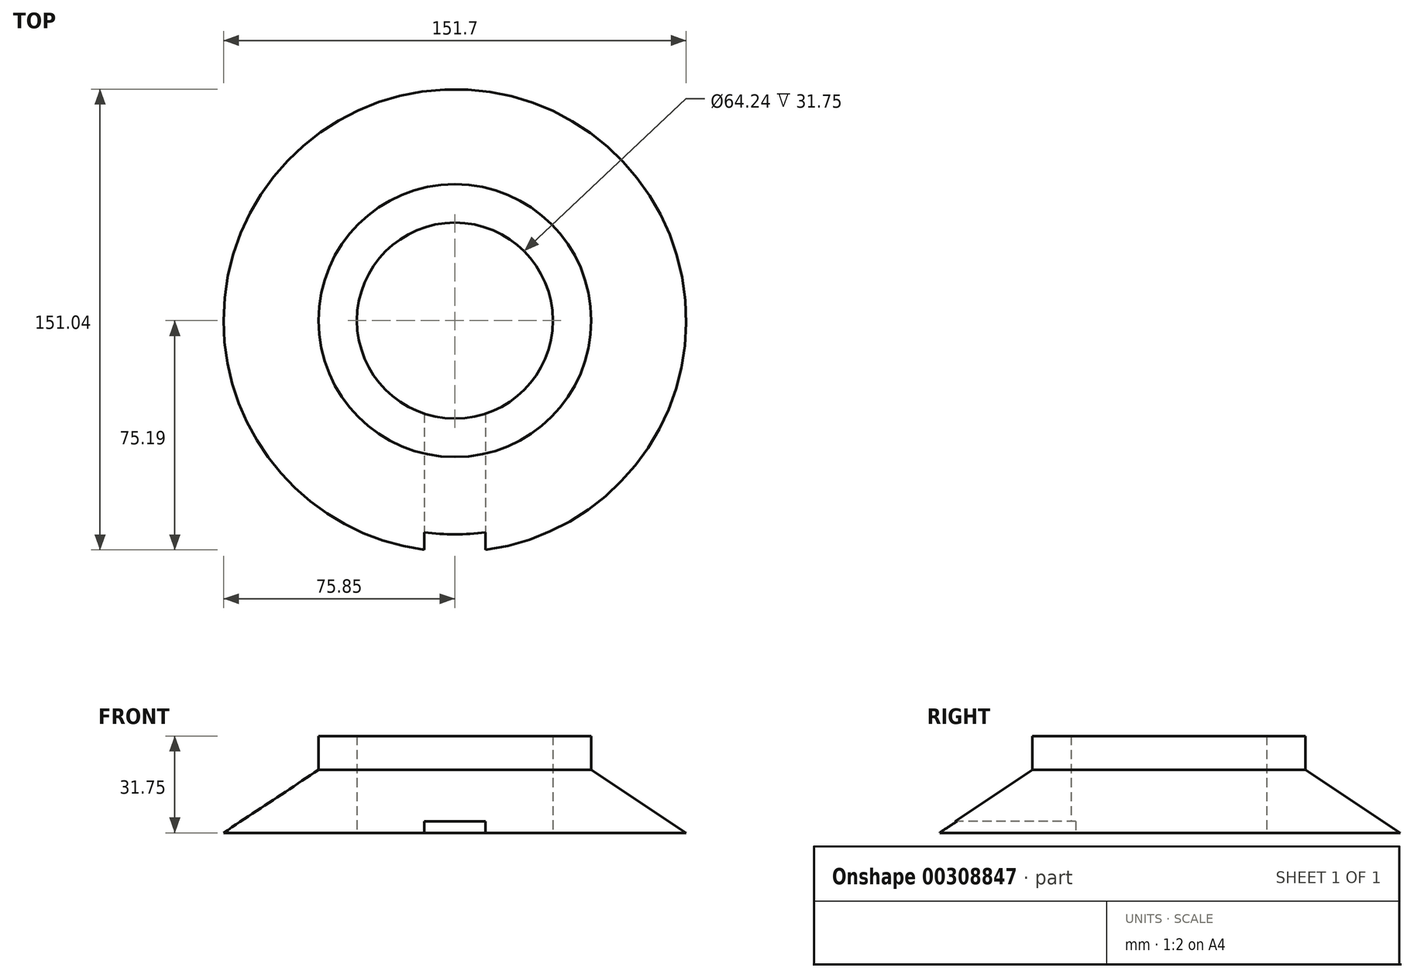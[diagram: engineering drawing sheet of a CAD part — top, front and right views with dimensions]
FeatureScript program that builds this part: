
annotation { "Feature Type Name" : "Feature", "Feature Type Description" : "" }
export const myFeature = defineFeature(function(context is Context, id is Id, definition is map)
    precondition{}
    {
        {
            var Q0;
            Q0=qCreatedBy(makeId("Front.planeOp"),FACE);
            var sketch = newSketch(context, id + "F0", { "sketchPlane" : qUnion([Q0])});
            skLineSegment(sketch, "E0.top", {"start": v(32.12, 31.75) * mm, "end": v(44.72, 31.75) * mm});
            skLineSegment(sketch, "E0.left", {"start": v(32.12, 0) * mm, "end": v(32.12, 31.75) * mm});
            skLineSegment(sketch, "E0.right", {"start": v(44.72, 20.63) * mm, "end": v(44.72, 31.75) * mm});
            skLineSegment(sketch, "E1", {"start": v(32.12, 0) * mm, "end": v(75.85, 0) * mm});
            skLineSegment(sketch, "E2", {"start": v(75.85, 0) * mm, "end": v(44.72, 20.63) * mm});
            skLineSegment(sketch, "E3", {"start": v(0, 0) * mm, "end": v(0, 70.2) * mm, "construction": true});
            skSolve(sketch);
        }
        {
            var Q0;
            Q0=makeQuery(id+"F0.imprint","IMPRINT",FACE,{"disambiguationData":[TD([[makeQuery(id+"F0.imprint","IMPRINT",EDGE,{"derivedFrom":sQuery(id+"F0.wireOp",EDGE,"E0.top")}),-1.0]])]});
            var Q1;
            Q1=sQuery(id+"F0.wireOp",EDGE,"E3");
            revolve(context, id + "F1", {"entities" : qUnion([Q0]), "axis" : qUnion([Q1]), "revolveType" : RevolveType.FULL});
        }
        {
            var Q0;
            Q0=makeQuery(id+"F1.opRevolve","SWEPT_FACE",FACE,{"disambiguationData":[OSD([sQuery(id+"F0.wireOp",EDGE,"E1")])]});
            var sketch = newSketch(context, id + "F2", { "sketchPlane" : qUnion([Q0])});
            skLineSegment(sketch, "E4.bottom", {"start": v(-9.99, 0) * mm, "end": v(9.99, 0) * mm});
            skLineSegment(sketch, "E4.top", {"start": v(-9.99, 84.1) * mm, "end": v(9.99, 84.1) * mm});
            skLineSegment(sketch, "E4.left", {"start": v(-9.99, 0) * mm, "end": v(-9.99, 84.1) * mm});
            skLineSegment(sketch, "E4.right", {"start": v(9.99, 0) * mm, "end": v(9.99, 84.1) * mm});
            skLineSegment(sketch, "E5", {"start": v(0, 0) * mm, "end": v(0, 91.19) * mm, "construction": true});
            skSolve(sketch);
        }
        {
            var Q0;
            {var subQ0=sQuery(id+"F2.wireOp",EDGE,"E4.left");var subQ1=sQuery(id+"F0.wireOp",EDGE,"E1");var subQ2=makeQuery(id+"F1.opRevolve","SWEPT_EDGE",EDGE,{"disambiguationData":[OSD([subQ1,sQuery(id+"F0.wireOp",EDGE,"E2")])]});var subQ3=makeQuery(id+"F2.imprint","INTERSECT",VERTEX,{"derivedFrom":[subQ2,subQ0]});Q0=makeQuery(id+"F2.imprint","IMPRINT",FACE,{"disambiguationData":[TD([[makeQuery(id+"F2.imprint","IMPRINT",EDGE,{"disambiguationData":[TD([[subQ3,1.0]])],"derivedFrom":subQ0}),-1.0]])]});}
            extrude(context, id + "F3", {"entities" : qUnion([Q0]), "operationType" : NewBodyOperationType.REMOVE, "oppositeDirection" : true, "depth" : 3.8 * mm});
        }
        {
            var Q0;
            Q0=qCreatedBy(makeId("Front.planeOp"),FACE);
            var sketch = newSketch(context, id + "F4", { "sketchPlane" : qUnion([Q0])});
            skLineSegment(sketch, "E6", {"start": v(0, 0) * mm, "end": v(0, 102.34) * mm, "construction": true});
            skSolve(sketch);
        }
    });
